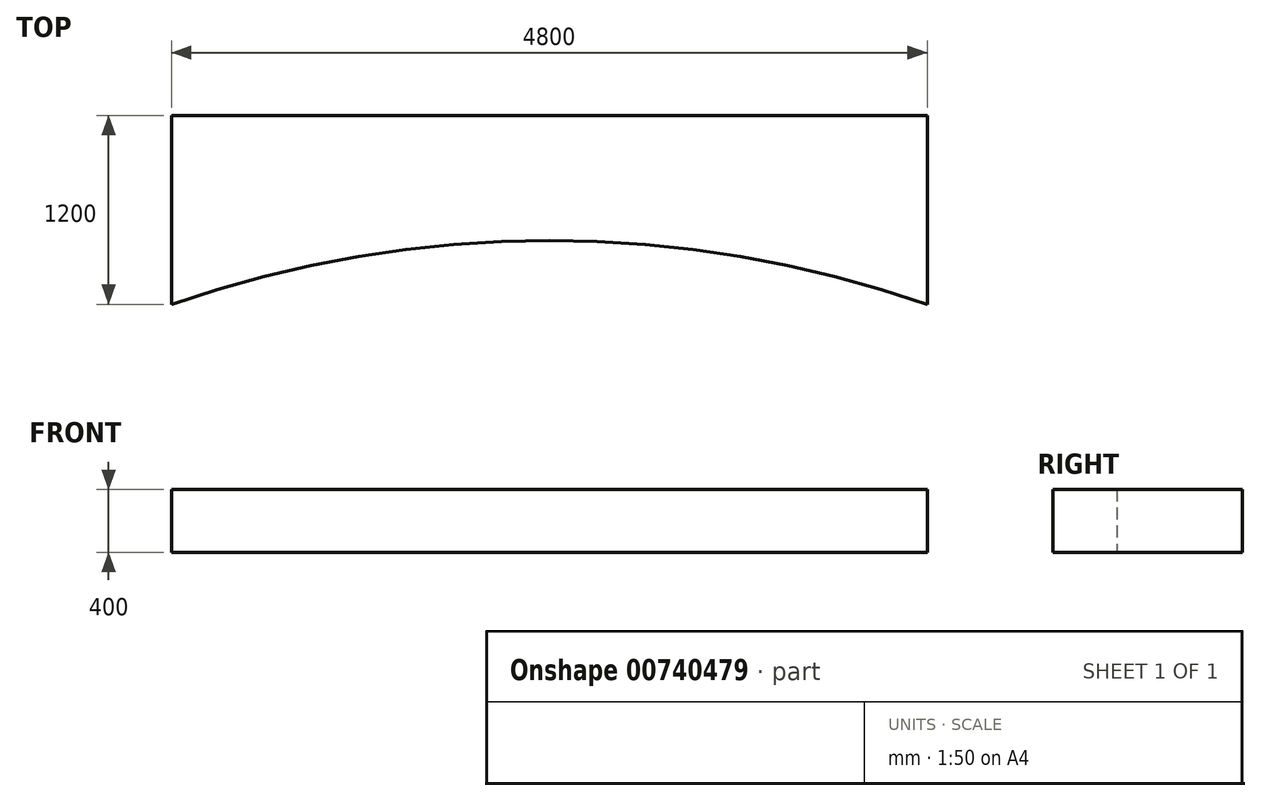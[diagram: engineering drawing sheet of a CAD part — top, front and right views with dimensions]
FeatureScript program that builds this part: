
annotation { "Feature Type Name" : "Feature", "Feature Type Description" : "" }
export const myFeature = defineFeature(function(context is Context, id is Id, definition is map)
    precondition{}
    {
        {
            var Q0;
            Q0=qCreatedBy(makeId("Top.planeOp"),FACE);
            var sketch = newSketch(context, id + "F0", { "sketchPlane" : qUnion([Q0])});
            skLineSegment(sketch, "E0.bottom", {"start": v(2400, 600) * mm, "end": v(-2400, 600) * mm});
            skLineSegment(sketch, "E0.left", {"start": v(2400, 600) * mm, "end": v(2400, -600) * mm});
            skLineSegment(sketch, "E0.right", {"start": v(-2400, 600) * mm, "end": v(-2400, -600) * mm});
            skPoint(sketch, "E0.middle", {"position": v(0, 0) * mm});
            skArc(sketch, "E1", {"start": v(2400, -600) * mm, "mid": v(0, -194.2) * mm, "end": v(-2400, -600) * mm});
            skPoint(sketch, "E1.second.point", {"position": v(0, -194.2) * mm});
            skSolve(sketch);
        }
        {
            var Q0;
            Q0=makeQuery(id+"F0.imprint","IMPRINT",FACE,{"disambiguationData":[TD([[makeQuery(id+"F0.imprint","IMPRINT",EDGE,{"derivedFrom":sQuery(id+"F0.wireOp",EDGE,"E0.bottom")}),1.0]])]});
            extrude(context, id + "F1", {"entities" : qUnion([Q0]), "depth" : 400 * mm, "offsetDistance" : 25 * mm});
        }
    });
